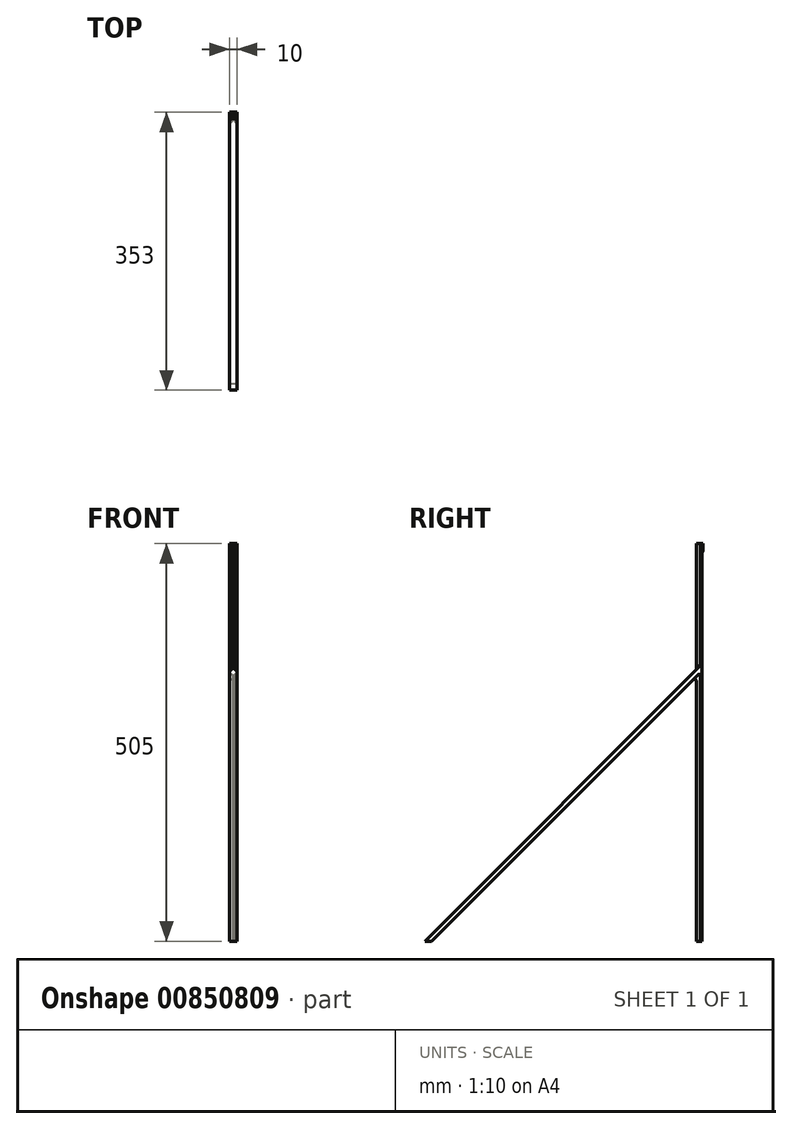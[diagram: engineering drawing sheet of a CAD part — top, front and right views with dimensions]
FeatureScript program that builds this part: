
annotation { "Feature Type Name" : "Feature", "Feature Type Description" : "" }
export const myFeature = defineFeature(function(context is Context, id is Id, definition is map)
    precondition{}
    {
        {
            var Q0;
            Q0=qCreatedBy(makeId("Top.planeOp"),FACE);
            var sketch = newSketch(context, id + "F0", { "sketchPlane" : qUnion([Q0])});
            skLineSegment(sketch, "E0", {"start": v(-1, 0) * mm, "end": v(-5, 0) * mm});
            skLineSegment(sketch, "E1", {"start": v(-5, 0) * mm, "end": v(-5, 2) * mm});
            skLineSegment(sketch, "E2", {"start": v(-5, 2) * mm, "end": v(5, 2) * mm});
            skLineSegment(sketch, "E3", {"start": v(5, 2) * mm, "end": v(5, 0) * mm});
            skLineSegment(sketch, "E4", {"start": v(5, 0) * mm, "end": v(1, 0) * mm});
            skLineSegment(sketch, "E5", {"start": v(1, 0) * mm, "end": v(1, -5) * mm});
            skLineSegment(sketch, "E6", {"start": v(1, -5) * mm, "end": v(-1, -5) * mm});
            skLineSegment(sketch, "E7", {"start": v(-1, -5) * mm, "end": v(-1, 0) * mm});
            skSolve(sketch);
        }
        {
            var Q0;
            Q0=qCreatedBy(makeId("Right.planeOp"),FACE);
            var sketch = newSketch(context, id + "F1", { "sketchPlane" : qUnion([Q0])});
            skLineSegment(sketch, "E8", {"start": v(0, 342) * mm, "end": v(0, 350) * mm});
            skLineSegment(sketch, "E9", {"start": v(-342, 0) * mm, "end": v(-350, 0) * mm});
            skLineSegment(sketch, "E10", {"start": v(-350, 0) * mm, "end": v(0, 350) * mm});
            skLineSegment(sketch, "E11", {"start": v(0, 342) * mm, "end": v(-342, 0) * mm});
            skLineSegment(sketch, "E12", {"start": v(0, -45) * mm, "end": v(0.1, -45) * mm});
            skLineSegment(sketch, "E13", {"start": v(3, 495) * mm, "end": v(3, 505) * mm});
            skLineSegment(sketch, "E14", {"start": v(3, 505) * mm, "end": v(2, 505) * mm});
            skLineSegment(sketch, "E15", {"start": v(2, 505) * mm, "end": v(1.97, 495) * mm});
            skLineSegment(sketch, "E16", {"start": v(3, 505) * mm, "end": v(3, 495) * mm});
            skLineSegment(sketch, "E17", {"start": v(3, 495) * mm, "end": v(1.97, 495) * mm});
            skSolve(sketch);
        }
        {
            var Q0;
            Q0=makeQuery(id+"F0.imprint","IMPRINT",FACE,{"disambiguationData":[TD([[makeQuery(id+"F0.imprint","IMPRINT",EDGE,{"derivedFrom":sQuery(id+"F0.wireOp",EDGE,"E0")}),-1.0]])]});
            extrude(context, id + "F2", {"entities" : qUnion([Q0]), "depth" : 505 * mm, "offsetDistance" : 25 * mm});
        }
        {
            var Q0;
            Q0=makeQuery(id+"F1.imprint","IMPRINT",FACE,{"disambiguationData":[TD([[makeQuery(id+"F1.imprint","IMPRINT",EDGE,{"derivedFrom":sQuery(id+"F1.wireOp",EDGE,"E8")}),1.0]])]});
            var Q1;
            Q1=makeQuery(id+"F1.imprint","IMPRINT",FACE,{"disambiguationData":[TD([[makeQuery(id+"F1.imprint","IMPRINT",EDGE,{"derivedFrom":sQuery(id+"F1.wireOp",EDGE,"E14")}),1.0]])]});
            extrude(context, id + "F3", {"entities" : qUnion([Q0, Q1]), "operationType" : NewBodyOperationType.ADD, "endBound" : BoundingType.SYMMETRIC, "depth" : 10 * mm, "offsetDistance" : 25 * mm});
        }
        {
            var Q0;
            Q0=makeQuery(id+"F2.opExtrude","SWEPT_EDGE",EDGE,{"disambiguationData":[OSD([sQuery(id+"F0.wireOp",EDGE,"E4"),sQuery(id+"F0.wireOp",EDGE,"E5")])]});
            var Q1;
            Q1=makeQuery(id+"F2.opExtrude","SWEPT_EDGE",EDGE,{"disambiguationData":[OSD([sQuery(id+"F0.wireOp",EDGE,"E0"),sQuery(id+"F0.wireOp",EDGE,"E7")])]});
            fillet(context, id + "F4", {"entities" : qUnion([Q0, Q1]), "radius" : 1 * mm, "tangentPropagation" : true, "allowEdgeOverflow" : false});
        }
        {
            var Q0;
            Q0=makeQuery(id+"F3.boolean.opBoolean","INTERSECT",EDGE,{"derivedFrom":[makeQuery(id+"F2.opExtrude","SWEPT_FACE",FACE,{"disambiguationData":[OSD([sQuery(id+"F0.wireOp",EDGE,"E6")])]}),makeQuery(id+"F3.opExtrude","SWEPT_FACE",FACE,{"disambiguationData":[OSD([sQuery(id+"F1.wireOp",EDGE,"E10")])]})]});
            fillet(context, id + "F5", {"entities" : qUnion([Q0]), "radius" : 3 * mm, "tangentPropagation" : true, "allowEdgeOverflow" : false});
        }
        {
            var Q0;
            Q0=makeQuery(id+"F3.boolean.opBoolean","INTERSECT",EDGE,{"derivedFrom":[makeQuery(id+"F2.opExtrude","SWEPT_FACE",FACE,{"disambiguationData":[OSD([sQuery(id+"F0.wireOp",EDGE,"E6")])]}),makeQuery(id+"F3.opExtrude","SWEPT_FACE",FACE,{"disambiguationData":[OSD([sQuery(id+"F1.wireOp",EDGE,"E11")])]})]});
            fillet(context, id + "F6", {"entities" : qUnion([Q0]), "radius" : 3 * mm, "tangentPropagation" : true, "allowEdgeOverflow" : false});
        }
        {
            var Q0;
            Q0=makeQuery(id+"F3.boolean.opBoolean","INTERSECT",EDGE,{"derivedFrom":[makeQuery(id+"F2.opExtrude","SWEPT_FACE",FACE,{"disambiguationData":[OSD([sQuery(id+"F0.wireOp",EDGE,"E2")])]}),makeQuery(id+"F3.opExtrude","SWEPT_FACE",FACE,{"disambiguationData":[OSD([sQuery(id+"F1.wireOp",EDGE,"E17")])]})]});
            fillet(context, id + "F7", {"entities" : qUnion([Q0]), "radius" : 1 * mm, "tangentPropagation" : true, "allowEdgeOverflow" : false});
        }
        {
            var Q0;
            Q0=makeQuery(id+"F3.boolean.opBoolean","INTERSECT",EDGE,{"derivedFrom":[makeQuery(id+"F2.opExtrude","SWEPT_FACE",FACE,{"disambiguationData":[OSD([sQuery(id+"F0.wireOp",EDGE,"E5")])]}),makeQuery(id+"F3.opExtrude","SWEPT_FACE",FACE,{"disambiguationData":[OSD([sQuery(id+"F1.wireOp",EDGE,"E10")])]})]});
            var Q1;
            Q1=makeQuery(id+"F3.boolean.opBoolean","INTERSECT",EDGE,{"derivedFrom":[makeQuery(id+"F2.opExtrude","SWEPT_FACE",FACE,{"disambiguationData":[OSD([sQuery(id+"F0.wireOp",EDGE,"E7")])]}),makeQuery(id+"F3.opExtrude","SWEPT_FACE",FACE,{"disambiguationData":[OSD([sQuery(id+"F1.wireOp",EDGE,"E10")])]})]});
            var Q2;
            {var subQ0=sQuery(id+"F1.wireOp",EDGE,"E10");Q2=makeQuery(id+"F3.boolean.opBoolean","SPLIT",EDGE,{"disambiguationData":[topologyDisambiguationEdgeConnected([makeQuery(id+"F2.opExtrude","SWEPT_FACE",FACE,{"disambiguationData":[OSD([sQuery(id+"F0.wireOp",EDGE,"E0")])]})])],"derivedFrom":makeQuery(id+"F3.opExtrude","SWEPT_EDGE",EDGE,{"disambiguationData":[OSD([sQuery(id+"F1.wireOp",EDGE,"E8"),subQ0])]})});}
            var Q3;
            Q3=makeQuery(id+"F3.boolean.opBoolean","INTERSECT",EDGE,{"derivedFrom":[makeQuery(id+"F2.opExtrude","SWEPT_FACE",FACE,{"disambiguationData":[OSD([sQuery(id+"F0.wireOp",EDGE,"E7")])]}),makeQuery(id+"F3.opExtrude","SWEPT_FACE",FACE,{"disambiguationData":[OSD([sQuery(id+"F1.wireOp",EDGE,"E11")])]})]});
            var Q4;
            {var subQ0=sQuery(id+"F1.wireOp",EDGE,"E11");Q4=makeQuery(id+"F3.boolean.opBoolean","SPLIT",EDGE,{"disambiguationData":[topologyDisambiguationEdgeConnected([makeQuery(id+"F2.opExtrude","SWEPT_FACE",FACE,{"disambiguationData":[OSD([sQuery(id+"F0.wireOp",EDGE,"E0")])]})])],"derivedFrom":makeQuery(id+"F3.opExtrude","SWEPT_EDGE",EDGE,{"disambiguationData":[OSD([sQuery(id+"F1.wireOp",EDGE,"E8"),subQ0])]})});}
            var Q5;
            Q5=makeQuery(id+"F3.boolean.opBoolean","INTERSECT",EDGE,{"derivedFrom":[makeQuery(id+"F2.opExtrude","SWEPT_FACE",FACE,{"disambiguationData":[OSD([sQuery(id+"F0.wireOp",EDGE,"E5")])]}),makeQuery(id+"F3.opExtrude","SWEPT_FACE",FACE,{"disambiguationData":[OSD([sQuery(id+"F1.wireOp",EDGE,"E11")])]})]});
            var Q6;
            {var subQ0=sQuery(id+"F1.wireOp",EDGE,"E11");Q6=makeQuery(id+"F3.boolean.opBoolean","SPLIT",EDGE,{"disambiguationData":[topologyDisambiguationEdgeConnected([makeQuery(id+"F2.opExtrude","SWEPT_FACE",FACE,{"disambiguationData":[OSD([sQuery(id+"F0.wireOp",EDGE,"E4")])]})])],"derivedFrom":makeQuery(id+"F3.opExtrude","SWEPT_EDGE",EDGE,{"disambiguationData":[OSD([sQuery(id+"F1.wireOp",EDGE,"E8"),subQ0])]})});}
            var Q7;
            {var subQ0=sQuery(id+"F1.wireOp",EDGE,"E10");Q7=makeQuery(id+"F3.boolean.opBoolean","SPLIT",EDGE,{"disambiguationData":[topologyDisambiguationEdgeConnected([makeQuery(id+"F2.opExtrude","SWEPT_FACE",FACE,{"disambiguationData":[OSD([sQuery(id+"F0.wireOp",EDGE,"E4")])]})])],"derivedFrom":makeQuery(id+"F3.opExtrude","SWEPT_EDGE",EDGE,{"disambiguationData":[OSD([sQuery(id+"F1.wireOp",EDGE,"E8"),subQ0])]})});}
            fillet(context, id + "F8", {"entities" : qUnion([Q0, Q1, Q2, Q3, Q4, Q5, Q6, Q7]), "radius" : 2 * mm, "tangentPropagation" : true, "allowEdgeOverflow" : false});
        }
    });
